# Revit family: SAE202
name_source: partatom
category: Lighting Fixtures
units: mm (PartAtom-declared; Revit-internal decimal feet)

## family parameters
Cut with Voids When Loaded = No
Host = Face
Light Source = Yes
OmniClass Number = 23.80.70.11.14.17
OmniClass Title = Direct/Indirect
Part Type = Normal
Room Calculation Point = No
Round Connector Dimension = Use Diameter
Shared = Yes

## types (5) — shared parameters
Apparent Load = 0 VA
Assembly Code = D5020200
Circuiting = 1 Circuit
Color Filter = 16777215
Default Elevation = 4' - 0"
Description = Recessed LED Wall/Slot
Diffuser = Blade Baffle with Overlay/Soft Glow Lens
Dimming Lamp Color Temperature Shift = <None>
Emit Shape Visible in Rendering = No
Emit from Rectangle Width = 0' - 4"
Glass = White Glass
Housing Material = Paint - Matte White
Is S/SG  Draywall = No
Is S/SG Grid = Yes
Lamp = LED's
Load Classification = Lighting
Manufacturer = Litecontrol
Model = SAE202
Photometric Notes = More IES files download on Photometric Web Link
Photometric Web File = SAE202-XX-2-S-SGL-CX-35K-D040.ies
Power Factor = 1
Shielding Position = Regressed Lens/Sheilding at Top
Tilt Angle = -90.00°
Type Comments = Lighting FIxture
URL = https://www.currentlighting.com
Voltage = 120 V
Warranty = 5-Years Warranty
Wattage Comments = 86 lumens/watt

## per-type parameters (varying)
| type | Emit from Rectangle Length | Row Length |
| SAE202-02 | 1' - 10" | 2' - 0" |
| SAE202-03 | 2' - 10" | 3' - 0" |
| SAE202-04 | 3' - 10" | 4' - 0" |
| SAE202-06 | 5' - 10" | 6' - 0" |
| SAE202-08 | 7' - 10" | 8' - 0" |

## geometry (parser evidence)
native form markers: Sweep x5
no freeform markers — native parametric forms only
